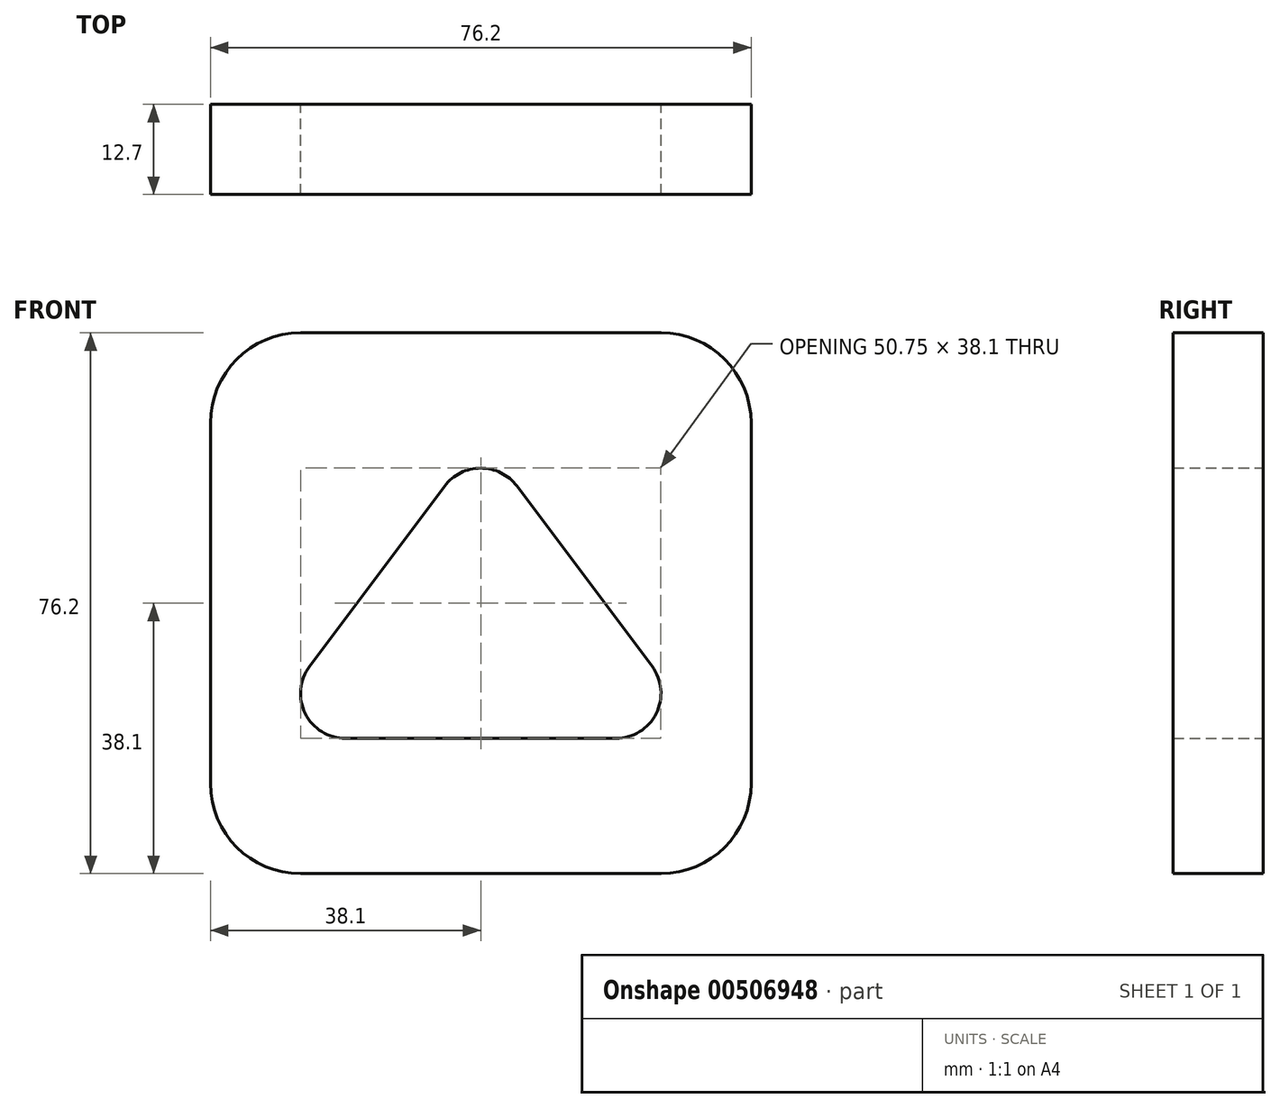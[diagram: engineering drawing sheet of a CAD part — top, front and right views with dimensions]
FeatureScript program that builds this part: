
annotation { "Feature Type Name" : "Feature", "Feature Type Description" : "" }
export const myFeature = defineFeature(function(context is Context, id is Id, definition is map)
    precondition{}
    {
        {
            var Q0;
            Q0=qCreatedBy(makeId("Front.planeOp"),FACE);
            var sketch = newSketch(context, id + "F0", { "sketchPlane" : qUnion([Q0])});
            skLineSegment(sketch, "E0", {"start": v(12.7, 0) * mm, "end": v(63.5, 0) * mm});
            skLineSegment(sketch, "E1", {"start": v(76.2, 12.7) * mm, "end": v(76.2, 63.5) * mm});
            skLineSegment(sketch, "E2", {"start": v(63.5, 76.2) * mm, "end": v(12.7, 76.2) * mm});
            skLineSegment(sketch, "E3", {"start": v(0, 63.5) * mm, "end": v(0, 12.7) * mm});
            skArc(sketch, "E4", {"start": v(13.97, 29.2) * mm, "mid": v(13.37, 22.56) * mm, "end": v(19.05, 19.05) * mm});
            skArc(sketch, "E5", {"start": v(57.15, 19.05) * mm, "mid": v(62.83, 22.56) * mm, "end": v(62.23, 29.21) * mm});
            skArc(sketch, "E6", {"start": v(43.18, 54.61) * mm, "mid": v(38.1, 57.15) * mm, "end": v(33.02, 54.61) * mm});
            skLineSegment(sketch, "E7", {"start": v(33.02, 54.61) * mm, "end": v(13.97, 29.2) * mm});
            skLineSegment(sketch, "E8", {"start": v(43.18, 54.61) * mm, "end": v(62.23, 29.21) * mm});
            skLineSegment(sketch, "E9", {"start": v(19.05, 19.05) * mm, "end": v(57.15, 19.05) * mm});
            skArc(sketch, "E10", {"start": v(12.7, 76.2) * mm, "mid": v(3.72, 72.48) * mm, "end": v(0, 63.5) * mm});
            skPoint(sketch, "E11.orphan", {"position": v(0, 76.2) * mm});
            skArc(sketch, "E12", {"start": v(76.2, 63.5) * mm, "mid": v(72.48, 72.48) * mm, "end": v(63.5, 76.2) * mm});
            skArc(sketch, "E13", {"start": v(0, 12.7) * mm, "mid": v(3.72, 3.72) * mm, "end": v(12.7, 0) * mm});
            skPoint(sketch, "E14.visualSharp", {"position": v(76.2, 0) * mm});
            skArc(sketch, "E14.filletArc", {"start": v(63.5, 0) * mm, "mid": v(72.48, 3.72) * mm, "end": v(76.2, 12.7) * mm});
            skSolve(sketch);
        }
        {
            var Q0;
            Q0=makeQuery(id+"F0.imprint","IMPRINT",FACE,{"disambiguationData":[TD([[makeQuery(id+"F0.imprint","IMPRINT",EDGE,{"derivedFrom":sQuery(id+"F0.wireOp",EDGE,"E0")}),1.0]])]});
            extrude(context, id + "F1", {"entities" : qUnion([Q0]), "depth" : 12.7 * mm});
        }
    });
